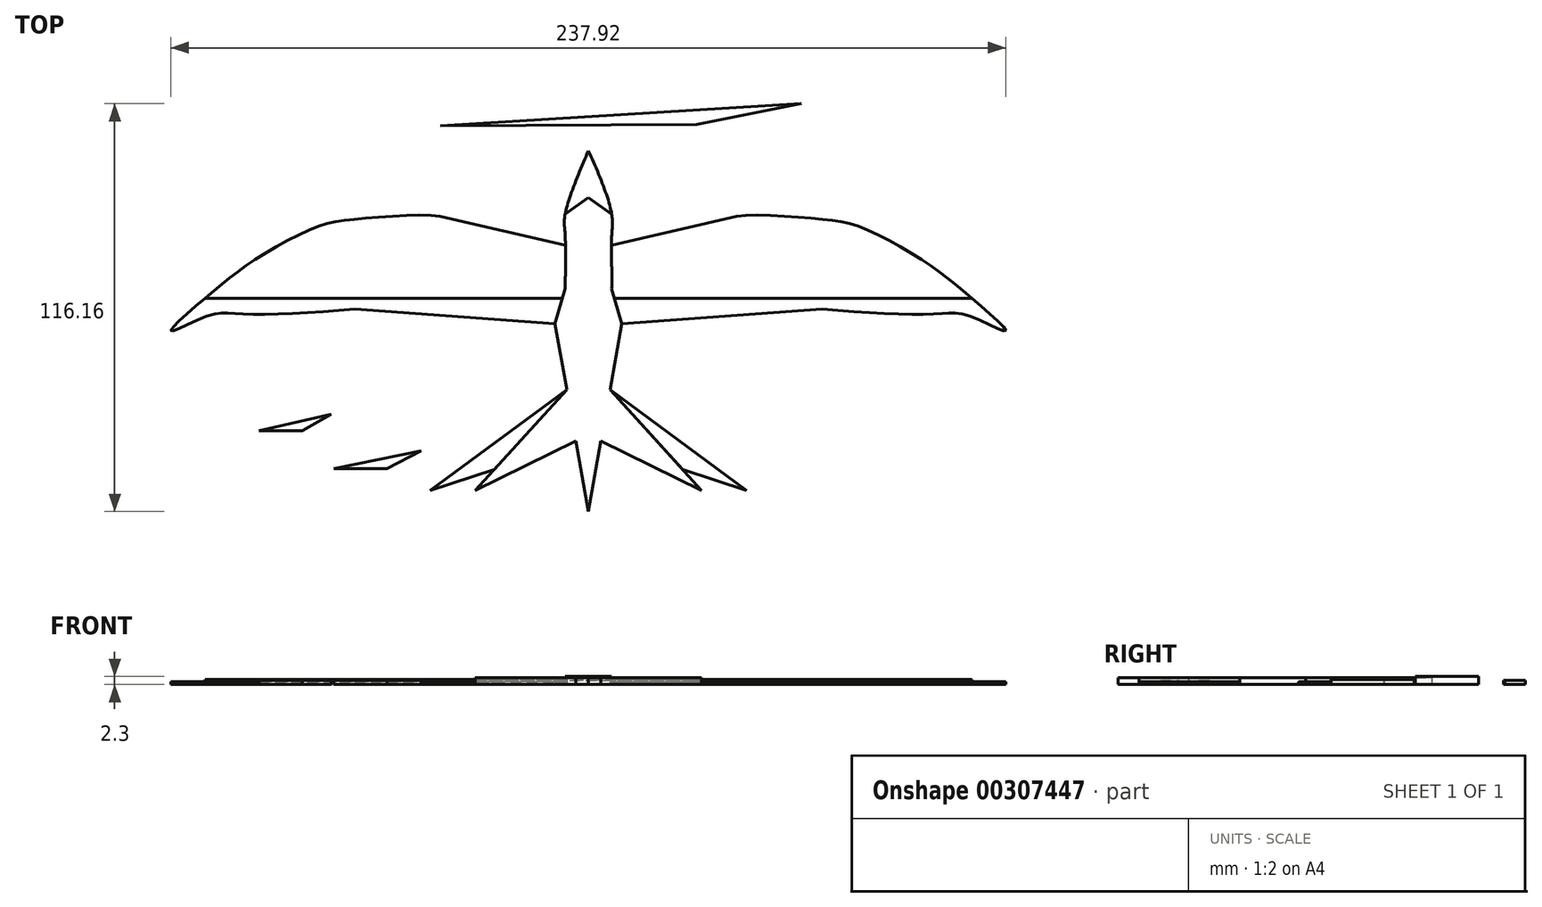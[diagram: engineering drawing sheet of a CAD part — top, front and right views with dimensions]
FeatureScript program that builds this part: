
annotation { "Feature Type Name" : "Feature", "Feature Type Description" : "" }
export const myFeature = defineFeature(function(context is Context, id is Id, definition is map)
    precondition{}
    {
        {
            var Q0;
            Q0=qCreatedBy(makeId("Top.planeOp"),FACE);
            var sketch = newSketch(context, id + "F0", { "sketchPlane" : qUnion([Q0])});
            skLineSegment(sketch, "E0", {"start": v(0, 0) * mm, "end": v(109.29, 0) * mm});
            skLineSegment(sketch, "E1", {"start": v(0, 28.7) * mm, "end": v(0, -38.93) * mm});
            skLineSegment(sketch, "E2.MirrorCS", {"start": v(0, 0) * mm, "end": v(-109.29, 0) * mm});
            skFitSpline(sketch, "E3", {"points": [v(-6.64, 2.75) * mm, v(-6.64, 18.3) * mm, v(-6.64, 23.92) * mm, v(0, 42.04) * mm], "startDerivative": vector(1.26, 40.48) * mm, "endDerivative": vector(19.76, 45.52) * mm});
            skFitSpline(sketch, "E4", {"points": [v(6.64, 2.75) * mm, v(6.64, 9.36) * mm, v(6.64, 17.86) * mm, v(6.64, 24) * mm, v(0, 42.04) * mm], "startDerivative": vector(0.3, 24.2) * mm, "endDerivative": vector(-24.29, 52.73) * mm});
            skLineSegment(sketch, "E5", {"start": v(-109.29, 0) * mm, "end": v(0, -8.05) * mm});
            skLineSegment(sketch, "E6", {"start": v(0, -8.05) * mm, "end": v(109.29, 0) * mm});
            skLineSegment(sketch, "E7", {"start": v(-9.5, -7.35) * mm, "end": v(0, -60.78) * mm});
            skLineSegment(sketch, "E8", {"start": v(-6.17, -26.1) * mm, "end": v(-32.25, -54.77) * mm});
            skLineSegment(sketch, "E9", {"start": v(-32.25, -54.77) * mm, "end": v(0, -38.93) * mm});
            skLineSegment(sketch, "E10", {"start": v(-6.17, -26.1) * mm, "end": v(-45.1, -54.77) * mm});
            skLineSegment(sketch, "E11", {"start": v(-45.1, -54.77) * mm, "end": v(-26.84, -48.83) * mm});
            skLineSegment(sketch, "E12", {"start": v(-6.64, 2.75) * mm, "end": v(0, 0) * mm});
            skLineSegment(sketch, "E13", {"start": v(6.64, 2.75) * mm, "end": v(0, 0) * mm});
            skFitSpline(sketch, "E14", {"points": [v(-42.3, 23.33) * mm, v(-64.97, 22.64) * mm, v(-77.68, 20.23) * mm, v(-96.52, 9.93) * mm, v(-109.29, 0) * mm, v(-118.9, -9.31) * mm, v(-107.91, -4.85) * mm, v(-99.32, -4.5) * mm, v(-66.61, -3.14) * mm], "startDerivative": vector(-96.4, 17.37) * mm, "endDerivative": vector(213.74, 18.11) * mm});
            skLineSegment(sketch, "E15", {"start": v(-42.3, 23.33) * mm, "end": v(-109.29, 0) * mm, "construction": true});
            skFitSpline(sketch, "E16", {"points": [v(-42.3, 23.33) * mm, v(-6.52, 15.07) * mm], "startDerivative": vector(35.77, -8.25) * mm, "endDerivative": vector(35.77, -8.25) * mm});
            skFitSpline(sketch, "E17.MirrorCS", {"points": [v(42.3, 23.33) * mm, v(6.52, 15.07) * mm], "startDerivative": vector(-35.77, -8.25) * mm, "endDerivative": vector(-35.77, -8.25) * mm});
            skLineSegment(sketch, "E18.MirrorCS", {"start": v(42.3, 23.33) * mm, "end": v(109.29, 0) * mm, "construction": true});
            skFitSpline(sketch, "E19.MirrorCS", {"points": [v(42.3, 23.33) * mm, v(64.97, 22.64) * mm, v(77.68, 20.23) * mm, v(96.52, 9.93) * mm, v(109.29, 0) * mm, v(118.9, -9.31) * mm, v(107.91, -4.85) * mm, v(99.32, -4.5) * mm, v(66.61, -3.14) * mm], "startDerivative": vector(96.4, 17.37) * mm, "endDerivative": vector(-213.74, 18.11) * mm});
            skLineSegment(sketch, "E20.MirrorCS", {"start": v(9.5, -7.35) * mm, "end": v(0, -60.78) * mm});
            skLineSegment(sketch, "E21.MirrorCS", {"start": v(6.17, -26.1) * mm, "end": v(32.25, -54.77) * mm});
            skLineSegment(sketch, "E22.MirrorCS", {"start": v(6.17, -26.1) * mm, "end": v(45.1, -54.77) * mm});
            skLineSegment(sketch, "E23.MirrorCS", {"start": v(32.25, -54.77) * mm, "end": v(0, -38.93) * mm});
            skLineSegment(sketch, "E24.MirrorCS", {"start": v(45.1, -54.77) * mm, "end": v(26.84, -48.83) * mm});
            skLineSegment(sketch, "E25", {"start": v(-9.5, -7.35) * mm, "end": v(-6.64, 2.75) * mm});
            skLineSegment(sketch, "E26", {"start": v(6.64, 2.75) * mm, "end": v(9.5, -7.35) * mm});
            skLineSegment(sketch, "E27", {"start": v(-6.64, 23.92) * mm, "end": v(0, 28.7) * mm});
            skLineSegment(sketch, "E28", {"start": v(0, 28.7) * mm, "end": v(6.64, 24) * mm});
            skLineSegment(sketch, "E29", {"start": v(-93.91, -37.78) * mm, "end": v(-81.59, -37.78) * mm});
            skLineSegment(sketch, "E30", {"start": v(-93.91, -37.78) * mm, "end": v(-73.31, -33.14) * mm});
            skLineSegment(sketch, "E31", {"start": v(-81.59, -37.78) * mm, "end": v(-73.31, -33.14) * mm});
            skLineSegment(sketch, "E32", {"start": v(-42.18, 49.1) * mm, "end": v(60.63, 55.38) * mm});
            skLineSegment(sketch, "E33", {"start": v(60.63, 55.38) * mm, "end": v(30.8, 49.5) * mm});
            skLineSegment(sketch, "E34", {"start": v(30.8, 49.5) * mm, "end": v(-42.18, 49.1) * mm});
            skLineSegment(sketch, "E35", {"start": v(-72.47, -48.6) * mm, "end": v(-57.49, -48.6) * mm});
            skLineSegment(sketch, "E36", {"start": v(-72.47, -48.6) * mm, "end": v(-47.68, -43.5) * mm});
            skLineSegment(sketch, "E37", {"start": v(-57.49, -48.6) * mm, "end": v(-47.68, -43.5) * mm});
            skSolve(sketch);
        }
        {
            var Q0;
            {var subQ0=sQuery(id+"F0.wireOp",EDGE,"640980cc-7635-4b82-95db-b256d293c04a");Q0=makeQuery(id+"F0.imprint","IMPRINT",FACE,{"disambiguationData":[TD([[makeQuery(id+"F0.imprint","IMPRINT",EDGE,{"derivedFrom":subQ0}),1.0]])]});}
            var Q1;
            {var subQ0=sQuery(id+"F0.wireOp",EDGE,"55000a13-7485-477a-a5ec-b682d487ac73");Q1=makeQuery(id+"F0.imprint","IMPRINT",FACE,{"disambiguationData":[TD([[makeQuery(id+"F0.imprint","IMPRINT",EDGE,{"derivedFrom":subQ0}),-1.0]])]});}
            var Q2;
            Q2=makeQuery(id+"F0.imprint","IMPRINT",FACE,{"disambiguationData":[TD([[makeQuery(id+"F0.imprint","IMPRINT",EDGE,{"derivedFrom":sQuery(id+"F0.wireOp",EDGE,"E3")}),-1.0]])]});
            var Q3;
            {var subQ3=sQuery(id+"F0.wireOp",EDGE,"E13");Q3=makeQuery(id+"F0.imprint","IMPRINT",FACE,{"disambiguationData":[TD([[makeQuery(id+"F0.imprint","IMPRINT",EDGE,{"derivedFrom":subQ3}),-1.0]])]});}
            var Q4;
            {var subQ0=sQuery(id+"F0.wireOp",EDGE,"E6");var subQ3=sQuery(id+"F0.wireOp",EDGE,"E20.MirrorCS");var subQ5=makeQuery(id+"F0.imprint","INTERSECT",VERTEX,{"derivedFrom":[subQ0,subQ3]});Q4=makeQuery(id+"F0.imprint","IMPRINT",FACE,{"disambiguationData":[TD([[makeQuery(id+"F0.imprint","IMPRINT",EDGE,{"disambiguationData":[TD([[subQ5,1.0]])],"derivedFrom":subQ0}),-1.0]])]});}
            var Q5;
            {var subQ0=sQuery(id+"F0.wireOp",EDGE,"E5");var subQ3=sQuery(id+"F0.wireOp",EDGE,"E7");var subQ5=makeQuery(id+"F0.imprint","INTERSECT",VERTEX,{"derivedFrom":[subQ0,subQ3]});Q5=makeQuery(id+"F0.imprint","IMPRINT",FACE,{"disambiguationData":[TD([[makeQuery(id+"F0.imprint","IMPRINT",EDGE,{"disambiguationData":[TD([[subQ5,-1.0]])],"derivedFrom":subQ0}),-1.0]])]});}
            var Q6;
            {var subQ0=sQuery(id+"F0.wireOp",EDGE,"E9");Q6=makeQuery(id+"F0.imprint","IMPRINT",FACE,{"disambiguationData":[TD([[makeQuery(id+"F0.imprint","IMPRINT",EDGE,{"derivedFrom":subQ0}),1.0]])]});}
            var Q7;
            {var subQ6=sQuery(id+"F0.wireOp",EDGE,"E23.MirrorCS");Q7=makeQuery(id+"F0.imprint","IMPRINT",FACE,{"disambiguationData":[TD([[makeQuery(id+"F0.imprint","IMPRINT",EDGE,{"derivedFrom":subQ6}),-1.0]])]});}
            var Q8;
            {var subQ0=sQuery(id+"F0.wireOp",EDGE,"E2.MirrorCS");var subQ5=sQuery(id+"F0.wireOp",EDGE,"E25");var subQ6=makeQuery(id+"F0.imprint","INTERSECT",VERTEX,{"derivedFrom":[subQ0,subQ5]});Q8=makeQuery(id+"F0.imprint","IMPRINT",FACE,{"disambiguationData":[TD([[makeQuery(id+"F0.imprint","IMPRINT",EDGE,{"disambiguationData":[TD([[subQ6,1.0]])],"derivedFrom":subQ5}),-1.0]])]});}
            var Q9;
            {var subQ1=sQuery(id+"F0.wireOp",EDGE,"E0");var subQ3=sQuery(id+"F0.wireOp",EDGE,"E26");var subQ4=makeQuery(id+"F0.imprint","INTERSECT",VERTEX,{"derivedFrom":[subQ1,subQ3]});Q9=makeQuery(id+"F0.imprint","IMPRINT",FACE,{"disambiguationData":[TD([[makeQuery(id+"F0.imprint","IMPRINT",EDGE,{"disambiguationData":[TD([[subQ4,-1.0]])],"derivedFrom":subQ3}),-1.0]])]});}
            var Q10;
            {var subQ0=sQuery(id+"F0.wireOp",EDGE,"E13");Q10=makeQuery(id+"F0.imprint","IMPRINT",FACE,{"disambiguationData":[TD([[makeQuery(id+"F0.imprint","IMPRINT",EDGE,{"derivedFrom":subQ0}),1.0]])]});}
            var Q11;
            {var subQ0=sQuery(id+"F0.wireOp",EDGE,"E12");Q11=makeQuery(id+"F0.imprint","IMPRINT",FACE,{"disambiguationData":[TD([[makeQuery(id+"F0.imprint","IMPRINT",EDGE,{"derivedFrom":subQ0}),-1.0]])]});}
            var Q12;
            {var subQ0=sQuery(id+"F0.wireOp",EDGE,"E20.MirrorCS");var subQ1=sQuery(id+"F0.wireOp",EDGE,"E7");var subQ2=makeQuery(id+"F0.imprint","INTERSECT",VERTEX,{"derivedFrom":[subQ1,subQ0]});Q12=makeQuery(id+"F0.imprint","IMPRINT",FACE,{"disambiguationData":[TD([[makeQuery(id+"F0.imprint","IMPRINT",EDGE,{"disambiguationData":[TD([[subQ2,1.0]])],"derivedFrom":subQ1}),1.0]])]});}
            extrude(context, id + "F1", {"entities" : qUnion([Q0, Q1, Q2, Q3, Q4, Q5, Q6, Q7, Q8, Q9, Q10, Q11, Q12]), "depth" : 2 * mm});
        }
        {
            var Q0;
            {var subQ3=sQuery(id+"F0.wireOp",EDGE,"E27");Q0=makeQuery(id+"F0.imprint","IMPRINT",FACE,{"disambiguationData":[TD([[makeQuery(id+"F0.imprint","IMPRINT",EDGE,{"derivedFrom":subQ3}),1.0]])]});}
            extrude(context, id + "F2", {"entities" : qUnion([Q0]), "depth" : 2.3 * mm});
        }
        {
            var Q0;
            {var subQ0=sQuery(id+"F0.wireOp",EDGE,"E19.MirrorCS");var subQ3=sQuery(id+"F0.wireOp",EDGE,"E17.MirrorCS");var subQ4=makeQuery(id+"F0.imprint","INTERSECT",VERTEX,{"derivedFrom":[subQ3,subQ0]});Q0=makeQuery(id+"F0.imprint","IMPRINT",FACE,{"disambiguationData":[TD([[makeQuery(id+"F0.imprint","IMPRINT",EDGE,{"disambiguationData":[TD([[subQ4,-1.0]])],"derivedFrom":subQ3}),1.0]])]});}
            var Q1;
            {var subQ0=sQuery(id+"F0.wireOp",EDGE,"E16");Q1=makeQuery(id+"F0.imprint","IMPRINT",FACE,{"disambiguationData":[TD([[makeQuery(id+"F0.imprint","IMPRINT",EDGE,{"derivedFrom":subQ0}),-1.0]])]});}
            extrude(context, id + "F3", {"entities" : qUnion([Q0, Q1]), "operationType" : NewBodyOperationType.ADD, "depth" : 1.5 * mm});
        }
        {
            var Q0;
            {var subQ0=sQuery(id+"F0.wireOp",EDGE,"E14");var subQ1=sQuery(id+"F0.wireOp",EDGE,"E5");var subQ3=makeQuery(id+"F0.imprint","INTERSECT",VERTEX,{"derivedFrom":[subQ1,subQ0]});Q0=makeQuery(id+"F0.imprint","IMPRINT",FACE,{"disambiguationData":[TD([[makeQuery(id+"F0.imprint","IMPRINT",EDGE,{"disambiguationData":[TD([[subQ3,1.0]])],"derivedFrom":subQ1}),-1.0]])]});}
            var Q1;
            {var subQ0=sQuery(id+"F0.wireOp",EDGE,"E19.MirrorCS");var subQ1=sQuery(id+"F0.wireOp",EDGE,"E6");var subQ3=makeQuery(id+"F0.imprint","INTERSECT",VERTEX,{"derivedFrom":[subQ1,subQ0]});Q1=makeQuery(id+"F0.imprint","IMPRINT",FACE,{"disambiguationData":[TD([[makeQuery(id+"F0.imprint","IMPRINT",EDGE,{"disambiguationData":[TD([[subQ3,-1.0]])],"derivedFrom":subQ1}),-1.0]])]});}
            var Q2;
            {var subQ0=sQuery(id+"F0.wireOp",EDGE,"E10");Q2=makeQuery(id+"F0.imprint","IMPRINT",FACE,{"disambiguationData":[TD([[makeQuery(id+"F0.imprint","IMPRINT",EDGE,{"derivedFrom":subQ0}),1.0]])]});}
            var Q3;
            {var subQ0=sQuery(id+"F0.wireOp",EDGE,"E22.MirrorCS");Q3=makeQuery(id+"F0.imprint","IMPRINT",FACE,{"disambiguationData":[TD([[makeQuery(id+"F0.imprint","IMPRINT",EDGE,{"derivedFrom":subQ0}),-1.0]])]});}
            var Q4;
            {var subQ2=sQuery(id+"F0.wireOp",EDGE,"E0");var subQ4=sQuery(id+"F0.wireOp",EDGE,"E26");var subQ5=makeQuery(id+"F0.imprint","INTERSECT",VERTEX,{"derivedFrom":[subQ2,subQ4]});Q4=makeQuery(id+"F0.imprint","IMPRINT",FACE,{"disambiguationData":[TD([[makeQuery(id+"F0.imprint","IMPRINT",EDGE,{"disambiguationData":[TD([[subQ5,-1.0]])],"derivedFrom":subQ2}),-1.0]])]});}
            var Q5;
            {var subQ2=sQuery(id+"F0.wireOp",EDGE,"E2.MirrorCS");var subQ4=sQuery(id+"F0.wireOp",EDGE,"E25");var subQ5=makeQuery(id+"F0.imprint","INTERSECT",VERTEX,{"derivedFrom":[subQ2,subQ4]});Q5=makeQuery(id+"F0.imprint","IMPRINT",FACE,{"disambiguationData":[TD([[makeQuery(id+"F0.imprint","IMPRINT",EDGE,{"disambiguationData":[TD([[subQ5,-1.0]])],"derivedFrom":subQ2}),1.0]])]});}
            extrude(context, id + "F4", {"entities" : qUnion([Q0, Q1, Q2, Q3, Q4, Q5]), "depth" : .8 * mm});
        }
        {
            var Q0;
            Q0=makeQuery(id+"F0.imprint","IMPRINT",FACE,{"disambiguationData":[TD([[makeQuery(id+"F0.imprint","IMPRINT",EDGE,{"derivedFrom":sQuery(id+"F0.wireOp",EDGE,"E29")}),1.0]])]});
            var Q1;
            Q1=makeQuery(id+"F0.imprint","IMPRINT",FACE,{"disambiguationData":[TD([[makeQuery(id+"F0.imprint","IMPRINT",EDGE,{"derivedFrom":sQuery(id+"F0.wireOp",EDGE,"E32")}),-1.0]])]});
            var Q2;
            Q2=makeQuery(id+"F0.imprint","IMPRINT",FACE,{"disambiguationData":[TD([[makeQuery(id+"F0.imprint","IMPRINT",EDGE,{"derivedFrom":sQuery(id+"F0.wireOp",EDGE,"E35")}),1.0]])]});
            extrude(context, id + "F5", {"entities" : qUnion([Q0, Q1, Q2]), "depth" : 1.2 * mm});
        }
    });
